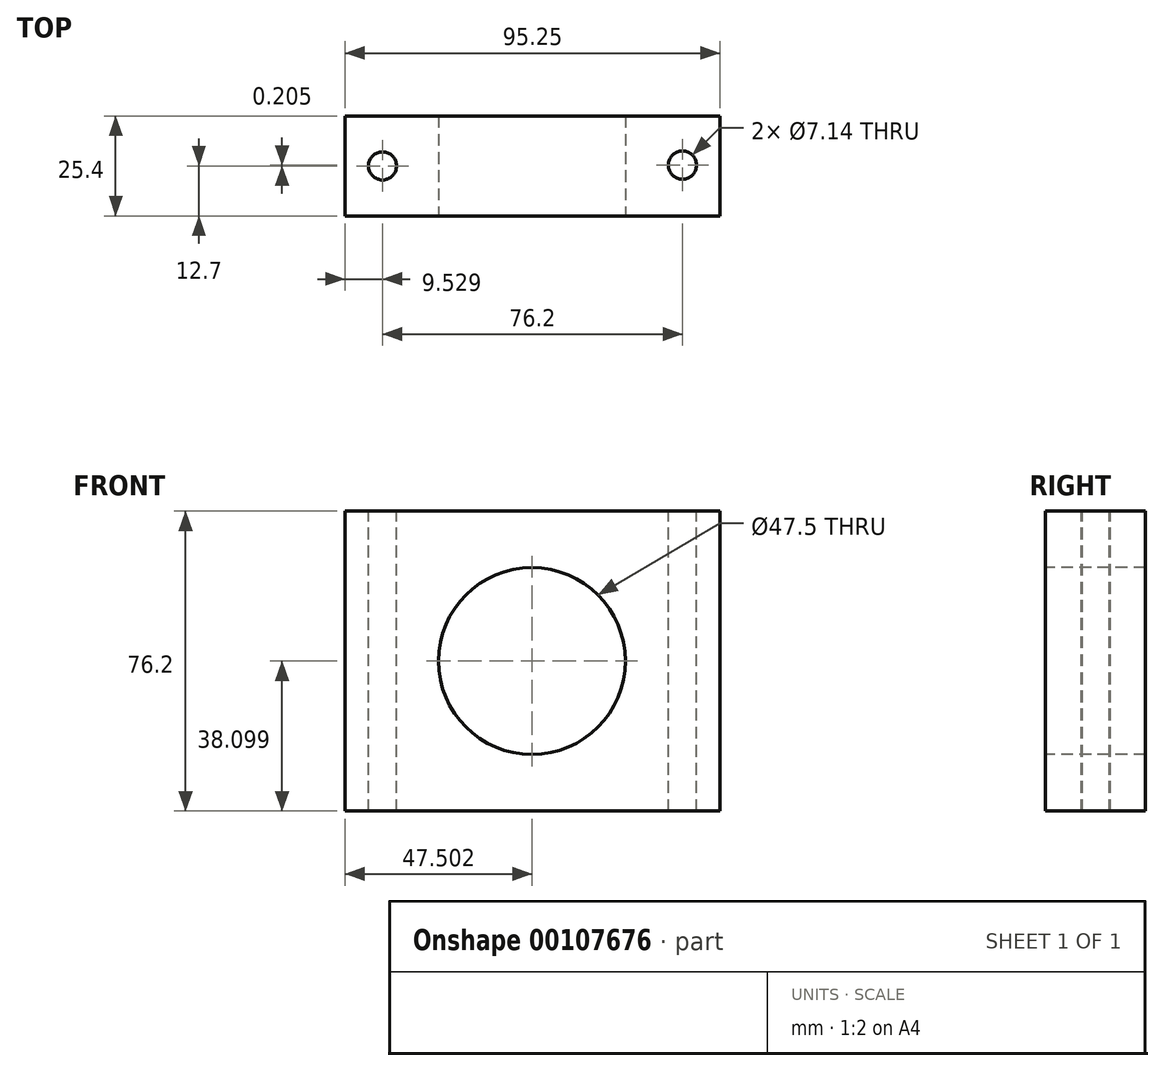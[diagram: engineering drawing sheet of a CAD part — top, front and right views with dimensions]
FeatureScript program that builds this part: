
annotation { "Feature Type Name" : "Feature", "Feature Type Description" : "" }
export const myFeature = defineFeature(function(context is Context, id is Id, definition is map)
    precondition{}
    {
        {
            var Q0;
            Q0=qCreatedBy(makeId("Front.planeOp"),FACE);
            var sketch = newSketch(context, id + "F0", { "sketchPlane" : qUnion([Q0])});
            skLineSegment(sketch, "E0", {"start": v(-50.05, -32.55) * mm, "end": v(45.2, -32.55) * mm});
            skLineSegment(sketch, "E1", {"start": v(45.2, -32.55) * mm, "end": v(45.2, 5.55) * mm});
            skLineSegment(sketch, "E2", {"start": v(45.2, 43.65) * mm, "end": v(45.2, 5.55) * mm});
            skLineSegment(sketch, "E3", {"start": v(-50.05, -32.55) * mm, "end": v(-50.05, 43.65) * mm});
            skLineSegment(sketch, "E4", {"start": v(-50.05, 43.65) * mm, "end": v(45.2, 43.65) * mm});
            skLineSegment(sketch, "E5", {"start": v(-2.42, 43.65) * mm, "end": v(-2.42, -32.55) * mm, "construction": true});
            skLineSegment(sketch, "E6", {"start": v(-50.05, 5.55) * mm, "end": v(45.2, 5.55) * mm, "construction": true});
            skCircle(sketch, "E7", {"center": v(-2.55, 5.55) * mm, "radius": 23.75 * mm});
            skSolve(sketch);
        }
        {
            var Q0;
            Q0=makeQuery(id+"F0.imprint","IMPRINT",FACE,{"disambiguationData":[TD([[makeQuery(id+"F0.imprint","IMPRINT",EDGE,{"derivedFrom":sQuery(id+"F0.wireOp",EDGE,"E0")}),1.0]])]});
            extrude(context, id + "F1", {"entities" : qUnion([Q0]), "oppositeDirection" : true, "depth" : 25.4 * mm});
        }
        {
            var Q0;
            Q0=makeQuery(id+"F1.opExtrude","SWEPT_FACE",FACE,{"disambiguationData":[OSD([sQuery(id+"F0.wireOp",EDGE,"E4")])]});
            var sketch = newSketch(context, id + "F2", { "sketchPlane" : qUnion([Q0])});
            skCircle(sketch, "E8", {"center": v(-40.52, 12.7) * mm, "radius": 3.57 * mm});
            skCircle(sketch, "E9", {"center": v(35.68, 12.9) * mm, "radius": 3.57 * mm});
            skSolve(sketch);
        }
        {
            var Q0;
            Q0=makeQuery(id+"F2.imprint","IMPRINT",FACE,{"disambiguationData":[TD([[makeQuery(id+"F2.imprint","IMPRINT",EDGE,{"derivedFrom":sQuery(id+"F2.wireOp",EDGE,"E8")}),1.0]])]});
            var Q1;
            Q1=makeQuery(id+"F2.imprint","IMPRINT",FACE,{"disambiguationData":[TD([[makeQuery(id+"F2.imprint","IMPRINT",EDGE,{"derivedFrom":sQuery(id+"F2.wireOp",EDGE,"E9")}),1.0]])]});
            extrude(context, id + "F3", {"entities" : qUnion([Q0, Q1]), "operationType" : NewBodyOperationType.REMOVE, "endBound" : BoundingType.THROUGH_ALL, "oppositeDirection" : true, "depth" : 25.4 * mm});
        }
    });
